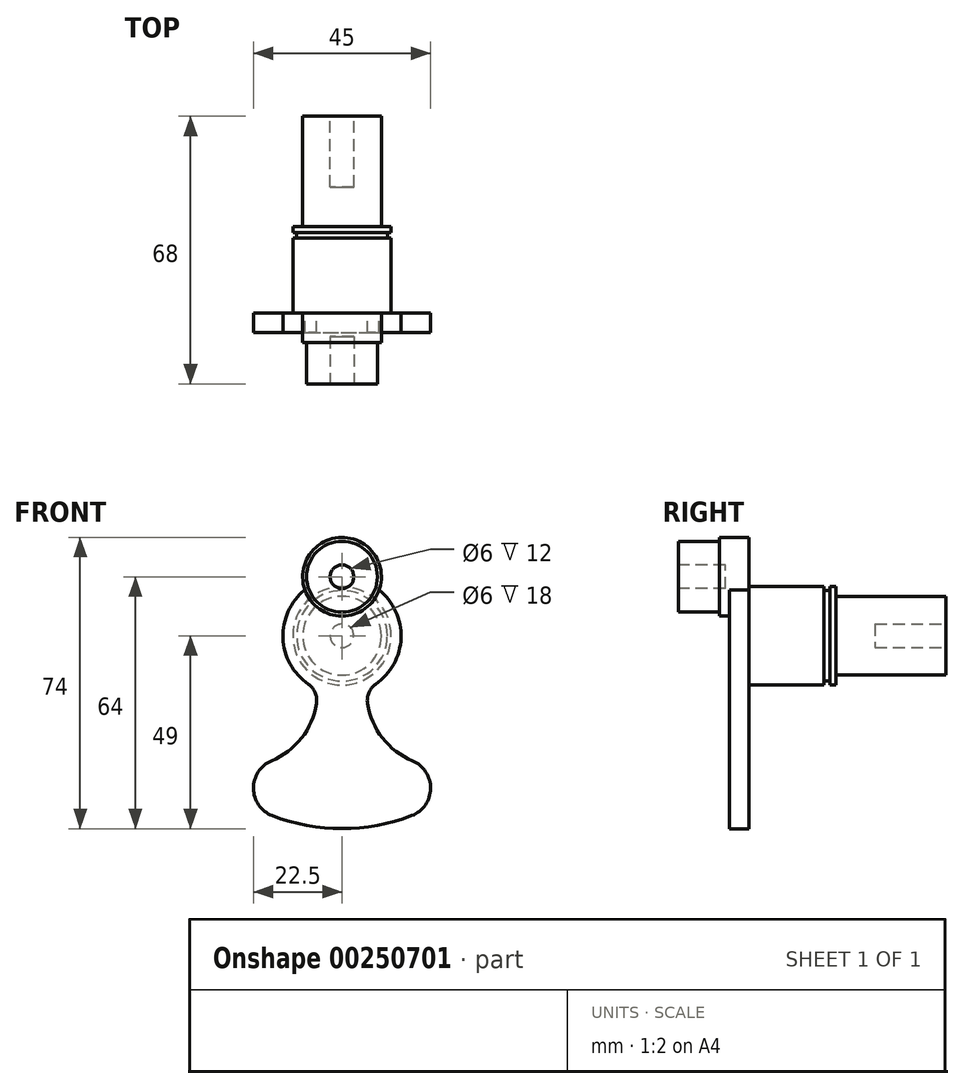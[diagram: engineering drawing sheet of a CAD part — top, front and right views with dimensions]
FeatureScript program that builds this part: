
annotation { "Feature Type Name" : "Feature", "Feature Type Description" : "" }
export const myFeature = defineFeature(function(context is Context, id is Id, definition is map)
    precondition{}
    {
        {
            var Q0;
            Q0=qCreatedBy(makeId("Right.planeOp"),FACE);
            var sketch = newSketch(context, id + "F0", { "sketchPlane" : qUnion([Q0])});
            skLineSegment(sketch, "E0", {"start": v(0, 0) * mm, "end": v(50, 0) * mm, "construction": true});
            skLineSegment(sketch, "E1", {"start": v(0, 12.5) * mm, "end": v(19, 12.5) * mm});
            skLineSegment(sketch, "E2", {"start": v(22, 12.5) * mm, "end": v(22, 10) * mm});
            skLineSegment(sketch, "E3", {"start": v(22, 10) * mm, "end": v(50, 10) * mm});
            skLineSegment(sketch, "E4", {"start": v(50, 10) * mm, "end": v(50, 0) * mm});
            skLineSegment(sketch, "E5", {"start": v(20.5, 12.5) * mm, "end": v(20.5, 11.5) * mm});
            skLineSegment(sketch, "E6", {"start": v(20.5, 11.5) * mm, "end": v(19, 11.5) * mm});
            skLineSegment(sketch, "E7", {"start": v(19, 11.5) * mm, "end": v(19, 12.5) * mm});
            skLineSegment(sketch, "E8.trimOffspring", {"start": v(20.5, 12.5) * mm, "end": v(22, 12.5) * mm});
            skLineSegment(sketch, "E9", {"start": v(0, 12.5) * mm, "end": v(0, 0) * mm});
            skLineSegment(sketch, "E10", {"start": v(0, 0) * mm, "end": v(50, 0) * mm});
            skSolve(sketch);
        }
        {
            var Q0;
            Q0=makeQuery(id+"F0.imprint","IMPRINT",FACE,{"disambiguationData":[TD([[makeQuery(id+"F0.imprint","IMPRINT",EDGE,{"derivedFrom":sQuery(id+"F0.wireOp",EDGE,"E1")}),-1.0]])]});
            var Q1;
            Q1=sQuery(id+"F0.wireOp",EDGE,"E10");
            revolve(context, id + "F1", {"entities" : qUnion([Q0]), "axis" : qUnion([Q1]), "revolveType" : RevolveType.FULL});
        }
        {
            var Q0;
            Q0=qCreatedBy(makeId("Front.planeOp"),FACE);
            var sketch = newSketch(context, id + "F2", { "sketchPlane" : qUnion([Q0])});
            skArc(sketch, "E11", {"start": v(-9.43, 11.67) * mm, "mid": v(-15, -0.54) * mm, "end": v(-8.56, -12.32) * mm});
            skArc(sketch, "E12", {"start": v(9.43, 11.67) * mm, "mid": v(0, 25) * mm, "end": v(-9.43, 11.67) * mm});
            skArc(sketch, "E13", {"start": v(0, -49) * mm, "mid": v(9, -48.16) * mm, "end": v(17.71, -45.69) * mm});
            skArc(sketch, "E14", {"start": v(17.71, -45.69) * mm, "mid": v(22.5, -38.8) * mm, "end": v(17.9, -31.78) * mm});
            skArc(sketch, "E15", {"start": v(6.48, -17.2) * mm, "mid": v(10.3, -25.97) * mm, "end": v(17.9, -31.78) * mm});
            skLineSegment(sketch, "E16", {"start": v(0, 52.55) * mm, "end": v(0, -53.15) * mm, "construction": true});
            skArc(sketch, "E17", {"start": v(8.56, -12.32) * mm, "mid": v(6.82, -14.45) * mm, "end": v(6.48, -17.2) * mm});
            skArc(sketch, "E18.MirrorCS", {"start": v(-8.56, -12.32) * mm, "mid": v(-6.82, -14.45) * mm, "end": v(-6.48, -17.2) * mm});
            skArc(sketch, "E19.MirrorCS", {"start": v(-6.48, -17.2) * mm, "mid": v(-10.3, -25.97) * mm, "end": v(-17.9, -31.78) * mm});
            skArc(sketch, "E20.MirrorCS", {"start": v(-17.71, -45.69) * mm, "mid": v(-22.5, -38.8) * mm, "end": v(-17.9, -31.78) * mm});
            skArc(sketch, "E21.MirrorCS", {"start": v(0, -49) * mm, "mid": v(-9, -48.16) * mm, "end": v(-17.71, -45.69) * mm});
            skArc(sketch, "E22.trimOffspring", {"start": v(8.56, -12.32) * mm, "mid": v(15, -0.54) * mm, "end": v(9.43, 11.67) * mm});
            skSolve(sketch);
        }
        {
            var Q0;
            Q0=qSketchRegion(id+"F2",true);
            extrude(context, id + "F3", {"entities" : qUnion([Q0]), "operationType" : NewBodyOperationType.ADD, "depth" : 5 * mm});
        }
        {
            var Q0;
            Q0=makeQuery(id+"F3.opExtrude","CAP_FACE",FACE,{"disambiguationData":[OSD([sQuery(id+"F2.wireOp",EDGE,"E11"),sQuery(id+"F2.wireOp",EDGE,"E12"),sQuery(id+"F2.wireOp",EDGE,"E13"),sQuery(id+"F2.wireOp",EDGE,"E14"),sQuery(id+"F2.wireOp",EDGE,"E15"),sQuery(id+"F2.wireOp",EDGE,"E17"),sQuery(id+"F2.wireOp",EDGE,"E18.MirrorCS"),sQuery(id+"F2.wireOp",EDGE,"E19.MirrorCS"),sQuery(id+"F2.wireOp",EDGE,"E20.MirrorCS"),sQuery(id+"F2.wireOp",EDGE,"E21.MirrorCS"),sQuery(id+"F2.wireOp",EDGE,"E22.trimOffspring")])],"isStart":false});
            var sketch = newSketch(context, id + "F4", { "sketchPlane" : qUnion([Q0])});
            skCircle(sketch, "E23", {"center": v(0, 15) * mm, "radius": 10 * mm});
            skSolve(sketch);
        }
        {
            var Q0;
            Q0=qSketchRegion(id+"F4",true);
            extrude(context, id + "F5", {"entities" : qUnion([Q0]), "operationType" : NewBodyOperationType.ADD, "depth" : 2.5 * mm});
        }
        {
            var Q0;
            Q0=makeQuery(id+"F5.opExtrude","CAP_FACE",FACE,{"disambiguationData":[OSD([sQuery(id+"F4.wireOp",EDGE,"E23")])],"isStart":false});
            var sketch = newSketch(context, id + "F6", { "sketchPlane" : qUnion([Q0])});
            skCircle(sketch, "E24", {"center": v(0, 15) * mm, "radius": 9 * mm});
            skSolve(sketch);
        }
        {
            var Q0;
            Q0=qSketchRegion(id+"F6",true);
            extrude(context, id + "F7", {"entities" : qUnion([Q0]), "operationType" : NewBodyOperationType.ADD, "depth" : 10.5 * mm});
        }
        {
            var Q0;
            Q0=makeQuery(id+"F7.opExtrude","CAP_FACE",FACE,{"disambiguationData":[OSD([sQuery(id+"F6.wireOp",EDGE,"E24")])],"isStart":false});
            var sketch = newSketch(context, id + "F8", { "sketchPlane" : qUnion([Q0])});
            skCircle(sketch, "E25", {"center": v(0, 15) * mm, "radius": 3 * mm});
            skSolve(sketch);
        }
        {
            var Q0;
            Q0=qSketchRegion(id+"F8",true);
            extrude(context, id + "F9", {"entities" : qUnion([Q0]), "operationType" : NewBodyOperationType.REMOVE, "oppositeDirection" : true, "depth" : 12 * mm});
        }
        {
            var Q0;
            Q0=makeQuery(id+"F1.opRevolve","SWEPT_FACE",FACE,{"disambiguationData":[OSD([sQuery(id+"F0.wireOp",EDGE,"E4")])]});
            var sketch = newSketch(context, id + "F10", { "sketchPlane" : qUnion([Q0])});
            skCircle(sketch, "E26", {"center": v(0, 0) * mm, "radius": 3 * mm});
            skSolve(sketch);
        }
        {
            var Q0;
            Q0=qSketchRegion(id+"F10",true);
            extrude(context, id + "F11", {"entities" : qUnion([Q0]), "operationType" : NewBodyOperationType.REMOVE, "oppositeDirection" : true, "depth" : 18 * mm});
        }
    });
